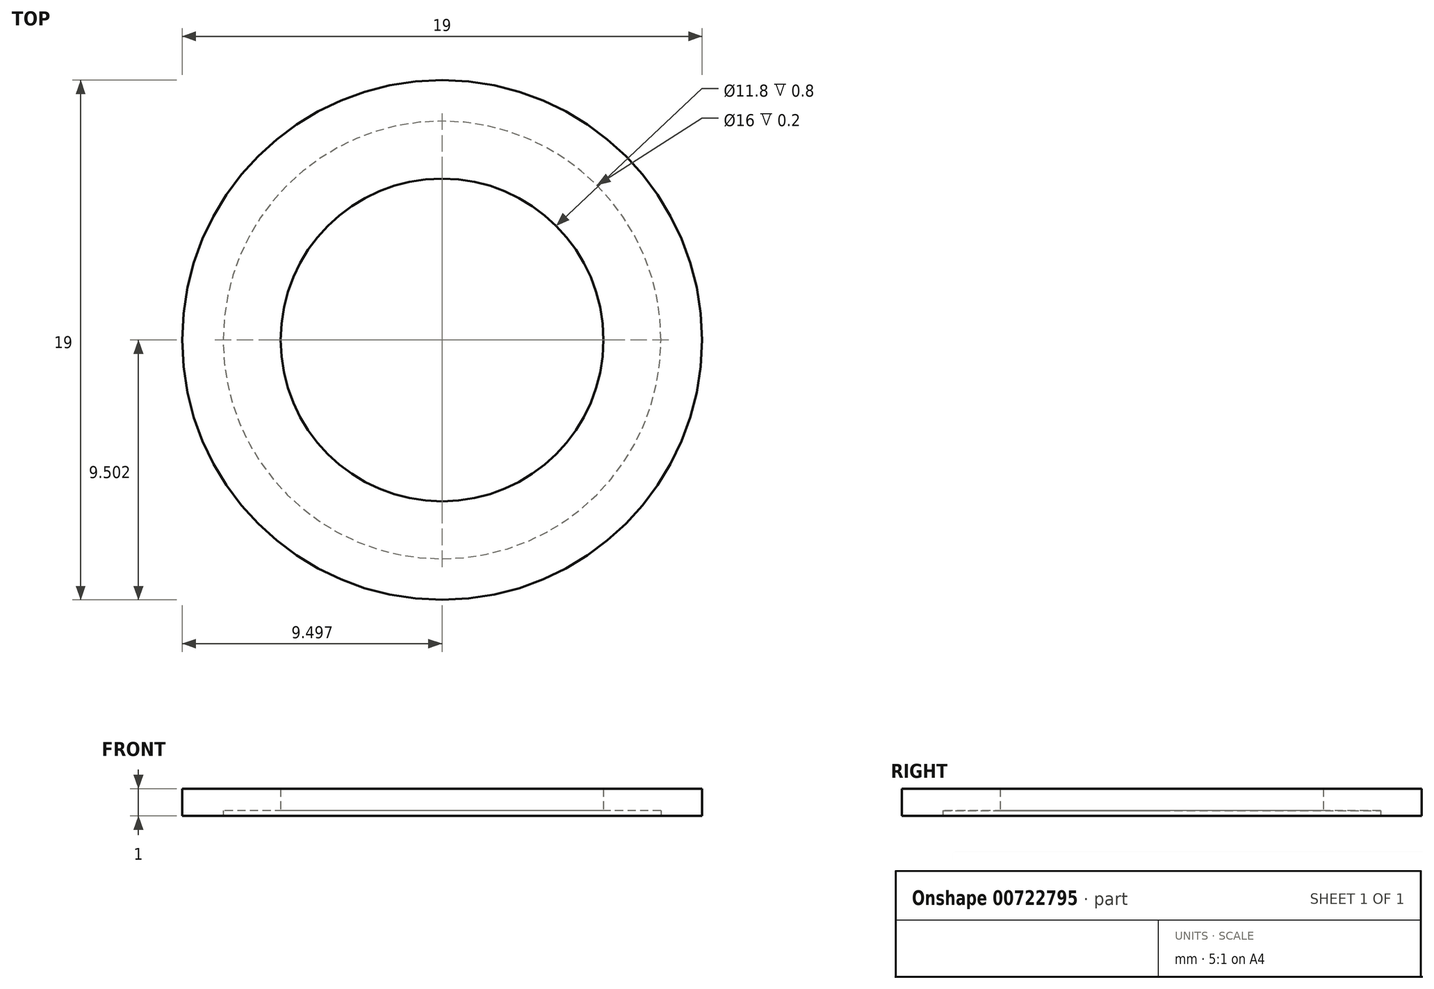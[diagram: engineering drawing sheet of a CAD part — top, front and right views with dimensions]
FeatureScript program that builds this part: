
annotation { "Feature Type Name" : "Feature", "Feature Type Description" : "" }
export const myFeature = defineFeature(function(context is Context, id is Id, definition is map)
    precondition{}
    {
        {
            var Q0;
            Q0=qCreatedBy(makeId("Top.planeOp"),FACE);
            var sketch = newSketch(context, id + "F0", { "sketchPlane" : qUnion([Q0])});
            skCircle(sketch, "E0", {"center": v(-21.2, 6.9) * mm, "radius": 5.9 * mm});
            skCircle(sketch, "E1", {"center": v(-21.2, 6.9) * mm, "radius": 8 * mm});
            skCircle(sketch, "E2", {"center": v(-21.2, 6.9) * mm, "radius": 9.5 * mm});
            skSolve(sketch);
        }
        {
            var Q0;
            Q0=makeQuery(id+"F0.imprint","IMPRINT",FACE,{"disambiguationData":[TD([[makeQuery(id+"F0.imprint","IMPRINT",EDGE,{"derivedFrom":sQuery(id+"F0.wireOp",EDGE,"E1")}),-1.0]])]});
            var Q1;
            Q1=makeQuery(id+"F0.imprint","IMPRINT",FACE,{"disambiguationData":[TD([[makeQuery(id+"F0.imprint","IMPRINT",EDGE,{"derivedFrom":sQuery(id+"F0.wireOp",EDGE,"E0")}),-1.0]])]});
            extrude(context, id + "F1", {"entities" : qUnion([Q0, Q1]), "depth" : 1 * mm, "offsetDistance" : 25 * mm});
        }
        {
            var Q0;
            Q0=makeQuery(id+"F0.imprint","IMPRINT",FACE,{"disambiguationData":[TD([[makeQuery(id+"F0.imprint","IMPRINT",EDGE,{"derivedFrom":sQuery(id+"F0.wireOp",EDGE,"E0")}),-1.0]])]});
            extrude(context, id + "F2", {"entities" : qUnion([Q0]), "operationType" : NewBodyOperationType.REMOVE, "depth" : .2 * mm, "offsetDistance" : 25 * mm});
        }
    });
